# Revit family: Vitra-Built-inStopValve(Exposedpart)-X-LineSeries-A41441
name_source: partatom
category: Plumbing Fixtures
revit_build: Autodesk Revit 2017 (Build: 20160225_1515(x64)
units: mm (PartAtom-declared; Revit-internal decimal feet)

## family parameters
Cut with Voids When Loaded = No
Host = Face
OmniClass Number = 23.45.55.17
OmniClass Title = Mixing Faucets
Part Type = Normal
Room Calculation Point = No
Round Connector Dimension = Use Diameter
Shared = Yes

## types (1)
- Stopvalve(Exposedpart)-Vitra-X-LineSeries-A41441
    Article No. (default) = A41441
    BIMobject category = Sanitary - Taps & Mixers
    CW Connection = Yes
    CWFU = 0
    Coating Material = Vitra-Chrome
    Connection Diameter (mm) = 10 mm  [stored 0.0328084 ft]
    Cost = 0 $
    Default Elevation = 850 mm  [stored 2.78871 ft]
    Depth(mm) = 44 mm  [stored 0.144357 ft]
    Description = To clean your product use a soft cloth soaked in alcohol or soap. Never use. acid or hydrochloric acid used to clean closed and floor and never use cleaning salt used to clean basin and sink.
    Design country = Turkey
    HW Connection = Yes
    HWFU = 0
    Height(mm) = 140 mm
    Hot Water Supply (max.) = 80 °C
    Hot Water temperature, factory set to = 38 °C
    IFC Classification = Valve
    Installation instructions = https://cdn.vitra.com.tr
    Main Material = Brass
    Manufacturer = Vitra
    Manufacturer name = Vitra
    Masterformat 2014 Code = 33 12 16
    Masterformat 2014 Description = Water Utility Distribution Valves
    Min. flow pressure of = 0.5 bar
    Model = A41441
    MountingType = Wall-mounted (exposed part)
    NBS Referans Description = Valves
    Nominal height = 0.000
    Nominal width = 0.000
    Number Of Connections = 1 mm  [stored 0.00328084 ft]
    OmniClass Code = 23-31 11 00
    OmniClass Description = Faucets
    Product SKU = A41441
    Product Type = Built-in Stop Valve(exposed part)
    Product certification = https://vitraglobal.com
    Product data url = https://www.vitraglobal.com
    Product family = X-Line
    Product group = Stop Valve (exposed part)
    Range of Hot Water Supply = 5 - 65 °C
    Range of flow pressure = 1 - 5 bar
    Technical description = https://www.vitra.com.tr
    Test Pressure = 16 bar
    UNSPSC Code = 301815
    UNSPSC Description = Sanitary ware
    URL = https://vitraglobal.com
    Uniclass 1.4 Code = L7117
    Uniclass 1.4 Description = Valves for water supply/distribution
    Uniclass 2.0 Description = Valves
    Uniclass 2015 Name = Valve products
    Uniformat II Code = 22 40 00
    Uniformat II Description = Plumbing Fixture
    WFU = 0
    Warranty Period (Year) = 7 Years
    Weight Net (kg) = 0,250
    Width(mm) = 50 mm
    Youtube = https://www.youtube.com

note: [stored X ft] marks values corroborated as IEEE doubles in the binary element streams (Revit-internal decimal feet)

## geometry (parser evidence)
native form markers: Sweep x3
no freeform markers — native parametric forms only
